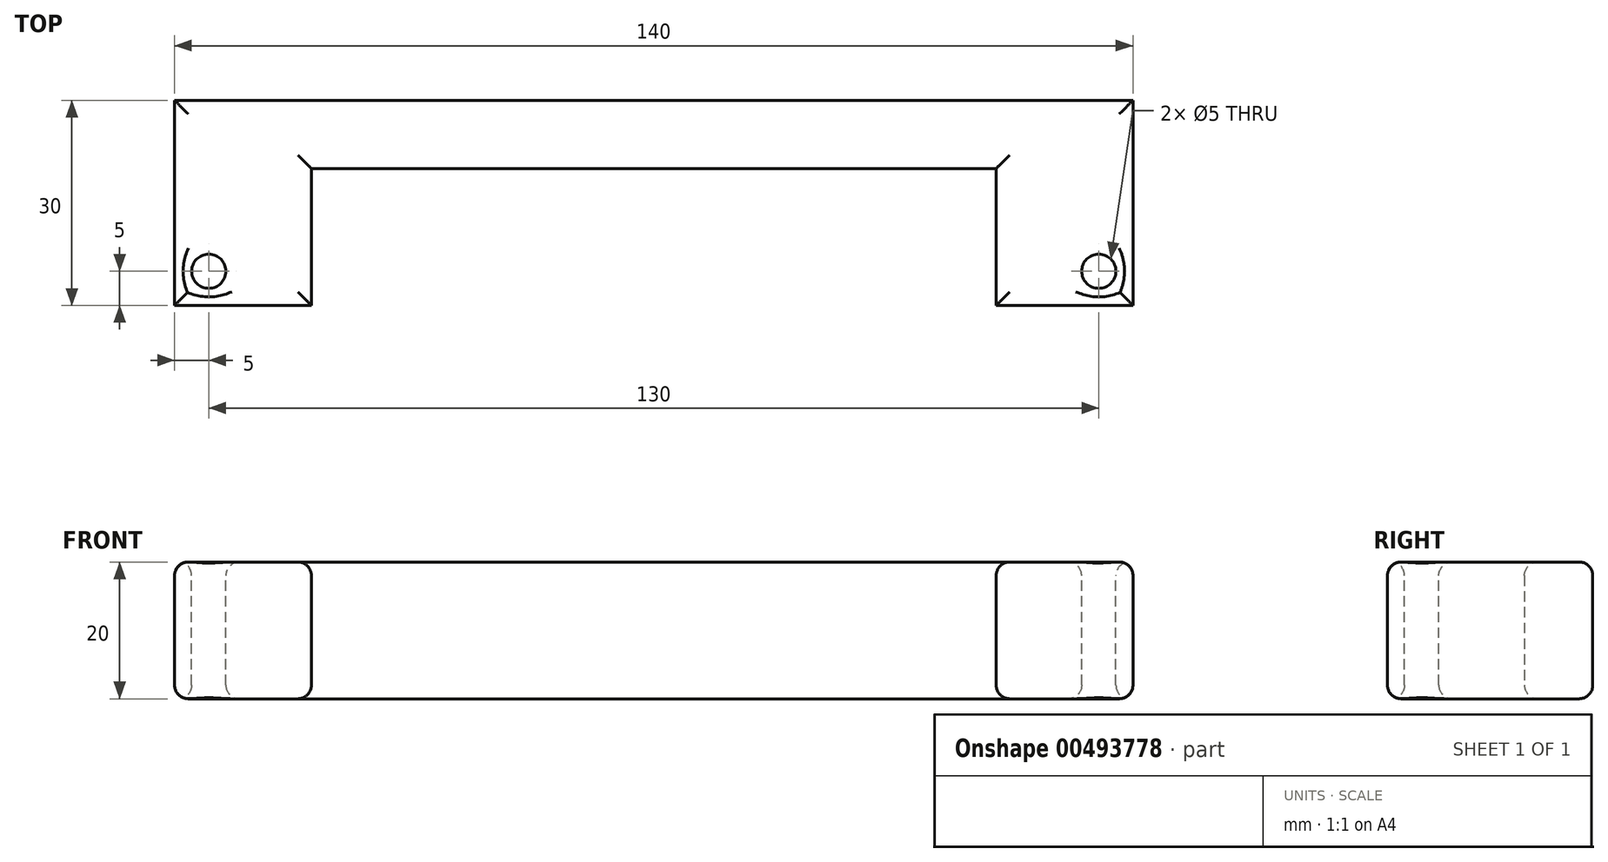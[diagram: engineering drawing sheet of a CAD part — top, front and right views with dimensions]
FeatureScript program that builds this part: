
annotation { "Feature Type Name" : "Feature", "Feature Type Description" : "" }
export const myFeature = defineFeature(function(context is Context, id is Id, definition is map)
    precondition{}
    {
        {
            var Q0;
            Q0=qCreatedBy(makeId("Top.planeOp"),FACE);
            var sketch = newSketch(context, id + "F0", { "sketchPlane" : qUnion([Q0])});
            skLineSegment(sketch, "E0", {"start": v(0, 30) * mm, "end": v(0, 20) * mm});
            skLineSegment(sketch, "E1", {"start": v(0, 20) * mm, "end": v(50, 20) * mm});
            skLineSegment(sketch, "E2", {"start": v(50, 20) * mm, "end": v(50, 0) * mm});
            skLineSegment(sketch, "E3", {"start": v(50, 0) * mm, "end": v(70, 0) * mm});
            skLineSegment(sketch, "E4", {"start": v(70, 0) * mm, "end": v(70, 30) * mm});
            skLineSegment(sketch, "E5", {"start": v(70, 30) * mm, "end": v(0, 30) * mm});
            skSolve(sketch);
        }
        {
            var Q0;
            Q0 = qSketchRegion(id + "F0", true);
            extrude(context, id + "F1", {"entities" : qUnion([Q0]), "depth" : 20 * mm});
        }
        {
            var Q0;
            Q0=makeQuery(id+"F1.opExtrude","CAP_FACE",FACE,{"disambiguationData":[OSD([sQuery(id+"F0.wireOp",EDGE,"E0"),sQuery(id+"F0.wireOp",EDGE,"E1"),sQuery(id+"F0.wireOp",EDGE,"E2"),sQuery(id+"F0.wireOp",EDGE,"E3"),sQuery(id+"F0.wireOp",EDGE,"E4"),sQuery(id+"F0.wireOp",EDGE,"E5")])],"isStart":false});
            var sketch = newSketch(context, id + "F2", { "sketchPlane" : qUnion([Q0])});
            skPoint(sketch, "E6", {"position": v(65, 5) * mm});
            skSolve(sketch);
        }
        {
            var Q0;
            Q0=sQuery(id+"F2.wireOp",VERTEX,"E6");
            var Q1;
            Q1=makeQuery(id+"F1.opExtrude","SWEPT_BODY",BODY,{"disambiguationData":[OSD([sQuery(id+"F0.wireOp",EDGE,"E0"),sQuery(id+"F0.wireOp",EDGE,"E1"),sQuery(id+"F0.wireOp",EDGE,"E2"),sQuery(id+"F0.wireOp",EDGE,"E3"),sQuery(id+"F0.wireOp",EDGE,"E4"),sQuery(id+"F0.wireOp",EDGE,"E5")])]});
            hole(context, id + "F3", {"style" : HoleStyle.SIMPLE, "endStyle" : HoleEndStyle.THROUGH, "holeDiameter" : 5 * mm, "isTappedThrough" : true, "tappedDepth" : 12 * mm, "tapClearance" : 3, "locations" : qUnion([Q0]), "scope" : qUnion([Q1])});
        }
        {
            var Q0;
            Q0=makeQuery(id+"F1.opExtrude","SWEPT_BODY",BODY,{"disambiguationData":[OSD([sQuery(id+"F0.wireOp",EDGE,"E0"),sQuery(id+"F0.wireOp",EDGE,"E1"),sQuery(id+"F0.wireOp",EDGE,"E2"),sQuery(id+"F0.wireOp",EDGE,"E3"),sQuery(id+"F0.wireOp",EDGE,"E4"),sQuery(id+"F0.wireOp",EDGE,"E5")])]});
            var Q1;
            Q1=makeQuery(id+"F1.opExtrude","SWEPT_FACE",FACE,{"disambiguationData":[OSD([sQuery(id+"F0.wireOp",EDGE,"E0")])]});
            mirror(context, id + "F4", {"operationType" : NewBodyOperationType.ADD, "entities" : qUnion([Q0]), "mirrorPlane" : qUnion([Q1])});
        }
        {
            var Q0;
            {var subQ0=makeQuery(id+"F1.opExtrude","CAP_FACE",FACE,{"disambiguationData":[OSD([sQuery(id+"F0.wireOp",EDGE,"E0"),sQuery(id+"F0.wireOp",EDGE,"E1"),sQuery(id+"F0.wireOp",EDGE,"E2"),sQuery(id+"F0.wireOp",EDGE,"E3"),sQuery(id+"F0.wireOp",EDGE,"E4"),sQuery(id+"F0.wireOp",EDGE,"E5")])],"isStart":false});Q0=makeQuery(id+"F4.boolean.opBoolean","MERGE",FACE,{"derivedFrom":[subQ0,makeQuery(id+"F4.opPattern","COPY",FACE,{"derivedFrom":subQ0,"instanceName":"1"})]});}
            var Q1;
            {var subQ0=makeQuery(id+"F1.opExtrude","CAP_FACE",FACE,{"disambiguationData":[OSD([sQuery(id+"F0.wireOp",EDGE,"E0"),sQuery(id+"F0.wireOp",EDGE,"E1"),sQuery(id+"F0.wireOp",EDGE,"E2"),sQuery(id+"F0.wireOp",EDGE,"E3"),sQuery(id+"F0.wireOp",EDGE,"E4"),sQuery(id+"F0.wireOp",EDGE,"E5")])],"isStart":true});Q1=makeQuery(id+"F4.boolean.opBoolean","MERGE",FACE,{"derivedFrom":[subQ0,makeQuery(id+"F4.opPattern","COPY",FACE,{"derivedFrom":subQ0,"instanceName":"1"})]});}
            fillet(context, id + "F5", {"entities" : qUnion([Q0, Q1]), "radius" : 2 * mm, "tangentPropagation" : true, "allowEdgeOverflow" : false});
        }
    });
